# Revit family: Indoor_Pendant Lamp_Santa&Cole_Estadio
name_source: partatom
category: Luminarias
revit_build: Autodesk Revit 2018 (Build: 20190510_1515(x64)
units: mm (PartAtom-declared; Revit-internal decimal feet)

## family parameters
Anfitrión = Cara
Compartido = No
Corte con vacíos al cargar = No
Cota de conector redondo = Diámetro de uso
Origen de luz = Sí
Punto de cálculo de habitación = No
Tipo de pieza = Normal

## types (6) — shared parameters
Archivo de red fotométrica = EST10.IES
Assembly Instructions - CE = https://www.santacole.com
Assembly Instructions - UL = https://www.santacole.com
Cambio de temperatura de color de luz atenuada = <Ninguno>
Carga aparente = 12 W
Elevación por defecto = 1219 mm
Energy Label = https://www.santacole.com
Fabricante = Santa & Cole
Filtro de color = 16777215
Lampshade Material = Santa&Cole - White Matte Finish
Load = 12 W
Manufacturer website = http://www.santacole.com
Modelo = Estadio
Technical Information = https://www.santacole.com
URL = https://www.santacole.com
Ángulo de inclinación = -90.00°

## per-type parameters (varying)
| type | 1 soporte | 1 soporte - Estadio 105 | 1 soporte - Estadio 150 | 1 soporte - Estadio 250 | 3 soportes - Estadio 105 | 3 soportes - Estadio 150 | 3 soportes - Estadio 250 | Code | Lampshade Height | Lampshade Type |
| Estadio 105 - 1 soporte | Sí | Sí | No | No | No | No | No | EST10+FSCG1
EST10+FSCG1
EST10+FSCG1 | 2263 mm | Lampara Estadio : Estadio 105 |
| Estadio 105 - 3 soportes | No | No | No | No | Sí | No | No | EST10+FSCG1
EST10+FSCG1
EST10+FSCG1 | 1207 mm | Lampara Estadio : Estadio 105 |
| Estadio 150 - 1 soporte | Sí | No | Sí | No | No | No | No | EST15+FSCG1 | 2263 mm | Lampara Estadio : Estadio 150 |
| Estadio 150 - 3 soportes | No | No | No | No | No | Sí | No | EST15+FSCG1 | 1207 mm | Lampara Estadio : Estadio 150 |
| Estadio 250 - 1 soporte | Sí | No | No | Sí | No | No | No | EST24+FSCG1 | 2263 mm | Lampara Estadio : Estadio 250 |
| Estadio 250 - 3 soportes | No | No | No | No | No | No | Sí | EST24+FSCG1 | 1207 mm | Lampara Estadio : Estadio 250 |

## geometry (parser evidence)
native form markers: Blend x4, Sweep x2
no freeform markers — native parametric forms only
